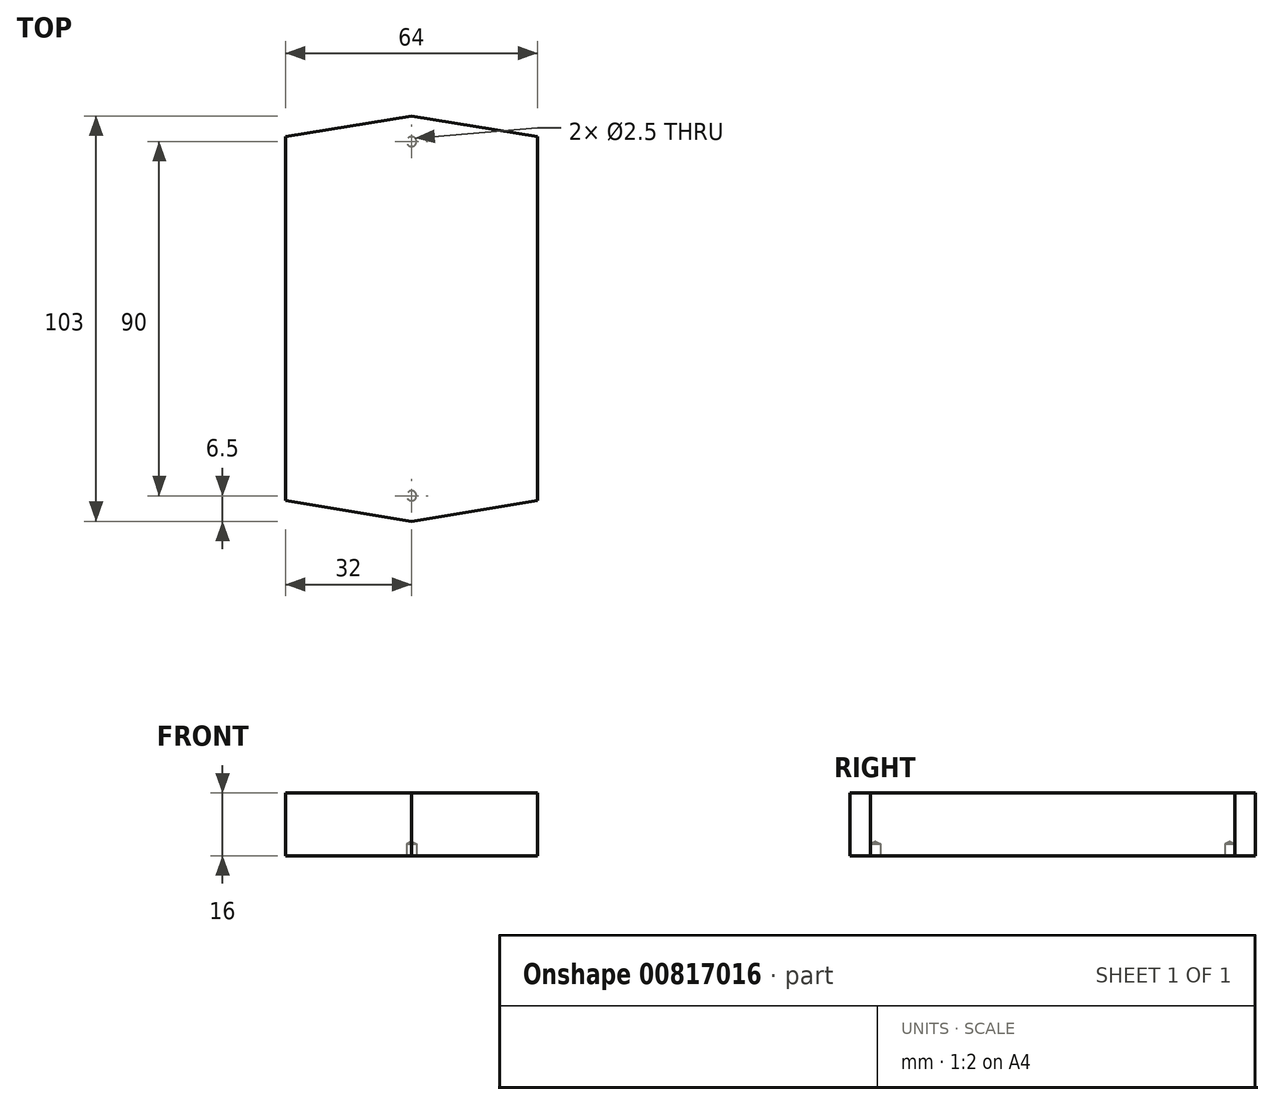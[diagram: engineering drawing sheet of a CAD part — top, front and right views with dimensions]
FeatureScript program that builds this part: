
annotation { "Feature Type Name" : "Feature", "Feature Type Description" : "" }
export const myFeature = defineFeature(function(context is Context, id is Id, definition is map)
    precondition{}
    {
        {
            var Q0;
            Q0=qCreatedBy(makeId("Top.planeOp"),FACE);
            var sketch = newSketch(context, id + "F0", { "sketchPlane" : qUnion([Q0])});
            skLineSegment(sketch, "E0", {"start": v(0, 0) * mm, "end": v(0, 51.5) * mm, "construction": true});
            skLineSegment(sketch, "E1", {"start": v(0, 51.5) * mm, "end": v(-32, 46.25) * mm});
            skLineSegment(sketch, "E2", {"start": v(-32, 46.25) * mm, "end": v(-32, 0) * mm});
            skLineSegment(sketch, "E3", {"start": v(0, 0) * mm, "end": v(-32, 0) * mm, "construction": true});
            skPoint(sketch, "E4", {"position": v(0, 45) * mm});
            skLineSegment(sketch, "E5.MirrorCS", {"start": v(0, 51.5) * mm, "end": v(32, 46.25) * mm});
            skLineSegment(sketch, "E6.MirrorCS", {"start": v(32, 46.25) * mm, "end": v(32, 0) * mm});
            skPoint(sketch, "E7.MirrorP", {"position": v(0, -45) * mm});
            skLineSegment(sketch, "E8.MirrorCS", {"start": v(-32, -46.25) * mm, "end": v(-32, 0) * mm});
            skLineSegment(sketch, "E9.MirrorCS", {"start": v(0, -51.5) * mm, "end": v(-32, -46.25) * mm});
            skLineSegment(sketch, "E10.MirrorCS", {"start": v(0, -51.5) * mm, "end": v(32, -46.25) * mm});
            skLineSegment(sketch, "E11.MirrorCS", {"start": v(32, -46.25) * mm, "end": v(32, 0) * mm});
            skSolve(sketch);
        }
        {
            var Q0;
            Q0=qSketchRegion(id+"F0",true);
            extrude(context, id + "F1", {"entities" : qUnion([Q0]), "depth" : 16 * mm});
        }
        {
            var Q0;
            Q0=sQuery(id+"F0.wireOp",VERTEX,"E7.MirrorP");
            var Q1;
            Q1=sQuery(id+"F0.wireOp",VERTEX,"E4");
            var Q2;
            Q2=makeQuery(id+"F1.opExtrude","SWEPT_BODY",BODY,{"disambiguationData":[OSD([sQuery(id+"F0.wireOp",EDGE,"E1"),sQuery(id+"F0.wireOp",EDGE,"E2"),sQuery(id+"F0.wireOp",EDGE,"E5.MirrorCS"),sQuery(id+"F0.wireOp",EDGE,"E6.MirrorCS"),sQuery(id+"F0.wireOp",EDGE,"E8.MirrorCS"),sQuery(id+"F0.wireOp",EDGE,"E9.MirrorCS"),sQuery(id+"F0.wireOp",EDGE,"E10.MirrorCS"),sQuery(id+"F0.wireOp",EDGE,"E11.MirrorCS")])]});
            hole(context, id + "F2", {"style" : HoleStyle.SIMPLE, "endStyle" : HoleEndStyle.BLIND, "oppositeDirection" : true, "holeDiameter" : 2.5 * mm, "holeDepth" : 3 * mm, "isTappedThrough" : true, "tappedDepth" : 3.5 * mm, "tapClearance" : 3, "locations" : qUnion([Q0, Q1]), "scope" : qUnion([Q2])});
        }
    });
